# Revit family: equip-sink-elkay-s-lustrrtone-lr1720-2219c
name_source: partatom
category: Plumbing Fixtures
units: mm (PartAtom-declared; Revit-internal decimal feet)

## family parameters
Always vertical = Yes
Cut with Voids When Loaded = No
OmniClass Number = 23.45.05.14.14.27
OmniClass Title = Service Sinks
Part Type = Normal
Room Calculation Point = No
Round Connector Dimension = Use Radius
Shared = No
Work Plane-Based = Yes

## types (8) — shared parameters
Assembly Code = D2010410
Back Faucet Hole One = Yes
Back Faucet Hole One Top = 0' - 0 1/2"
Back Faucet Hole One to CL = 0' - 2"
Back Faucet Hole Two = Yes
Back Faucet Hole Two Top = 0' - 0 1/2"
Bowl Drain Location FB = 0' - 7"
Bowl Width = 1' - 2"
CW Flow Rate = 2 GPM
Default Elevation = 3' - 0"
Description = Lustertone Single Bowl Sink
Drain Material = Metal - Steel - Stainless - Chrome
Drain Part = LK18
Faucet Hole CL One to Two = 0' - 4"
Faucet Material = Metal - Steel - Stainless - Chrome
Faucet Part = LK406GN04T4
Faucet Plan = Yes
HW Flow Rate = 2 GPM
Manufacturer = Elkay Manufacturing
MasterFormat Number = 22.42.16.16
MasterFormat Title = Commercial Sinks
Nominal Dia = 0' - 0 3/8"
Nominal Radius = 0' - 0 3/16"
OmniClass Code = 23.45.05.14.14.27
OmniClass Title = Service Sinks
Sanitary Flow Rate = 10 GPM
Sanitary Installation Depth from Top Sink_CounterTop = 1' - 2 1/2"
Sanitary Nominal Dia = 0' - 1 1/2"
Sanitary Nominal Radius = 0' - 0 3/4"
Sink Material = Metal - Steel - Stainless - Chrome
Specification Sheet URL = http://www.elkayusa.com
Stem Material = Metal - Steel
URL = www.elkayusa.com
Wall Face to Back Face of Bowl = 0' - 6 1/4"
Wall Face to Drain Trap CL = 0' - 11 1/32"

## per-type parameters (varying)
| type | Back Faucet CL to Back | Bowl Depth | Bowl Length | Drain CL LR to Left Bowl Edge | Minimum Cabinet Width | Sink Ledge Back Width | Sink Ledge Back Width Hidden | Sink Ledge Front Width | Sink Ledge Front Width Hidden | Sink Ledge Left Width | Sink Ledge Left Width Hidden | Sink Ledge Right Width | Sink Ledge Right Width Hidden | Sink Length | Sink Part | Sink Width |
| LR1720C | 0' - 2 1/4" | 0' - 7 5/8" | 1' - 2" | 0' - 7" | 24" | 0' - 4 1/4" | 0' - 4 1/4" | 0' - 1 3/4" | 0' - 1 3/4" | 0' - 1 1/2" | 0' - 1 1/2" | 0' - 1 1/2" | 0' - 1 1/2" | 1' - 5" | LR17202 | 1' - 8" |
| LRAD172055C | 0' - 2 1/4" | 0' - 5 1/2" | 1' - 2" | 0' - 7" | 24" | 0' - 4 1/4" | 0' - 4 1/4" | 0' - 1 3/4" | 0' - 1 3/4" | 0' - 1 1/2" | 0' - 1 1/2" | 0' - 1 1/2" | 0' - 1 1/2" | 1' - 5" | LR1720552 | 1' - 8" |
| LRAD172065C | 0' - 2 1/4" | 0' - 6 1/2" | 1' - 2" | 0' - 7" | 24" | 0' - 4 1/4" | 0' - 4 1/4" | 0' - 1 3/4" | 0' - 1 3/4" | 0' - 1 1/2" | 0' - 1 1/2" | 0' - 1 1/2" | 0' - 1 1/2" | 1' - 5" | LR1720652 | 1' - 8" |
| LRAD172060C | 0' - 2 1/4" | 0' - 6" | 1' - 2" | 0' - 7" | 24" | 0' - 4 1/4" | 0' - 4 1/4" | 0' - 1 3/4" | 0' - 1 3/4" | 0' - 1 1/2" | 0' - 1 1/2" | 0' - 1 1/2" | 0' - 1 1/2" | 1' - 5" | LR1720602 | 1' - 8" |
| LR2219C | 0' - 2 1/4" | 0' - 7 5/8" | 1' - 6" | 0' - 9" | 24" | 0' - 4" | 0' - 4" | 0' - 1 1/2" | 0' - 1 1/2" | 0' - 2" | 0' - 2" | 0' - 2" | 0' - 2" | 1' - 10" | LR22192 | 1' - 7 1/2" |
| LRAD221955C | 0' - 2 1/4" | 0' - 5 1/2" | 1' - 6" | 0' - 9" | 30" | 0' - 4" | 0' - 4" | 0' - 1 1/2" | 0' - 1 1/2" | 0' - 2" | 0' - 2" | 0' - 2" | 0' - 2" | 1' - 10" | LRAD2219552 | 1' - 7 1/2" |
| LRAD221965C | 0' - 2" | 0' - 6 1/2" | 1' - 6" | 0' - 9" | 30" | 0' - 4" | 0' - 4" | 0' - 1 1/2" | 0' - 1 1/2" | 0' - 2" | 0' - 2" | 0' - 2" | 0' - 2" | 1' - 10" | LRAD2219652 | 1' - 7 1/2" |
| LRAD221960C | 0' - 2 1/4" | 0' - 6" | 1' - 6" | 0' - 9" | 30" | 0' - 4" | 0' - 4" | 0' - 1 1/2" | 0' - 1 1/2" | 0' - 2" | 0' - 2" | 0' - 2" | 0' - 2" | 1' - 10" | LRAD2219602 | 1' - 7 1/2" |

note: column(s) folded — value = type name in every type: Model

## geometry (parser evidence)
native form markers: Sweep x10
no freeform markers — native parametric forms only
